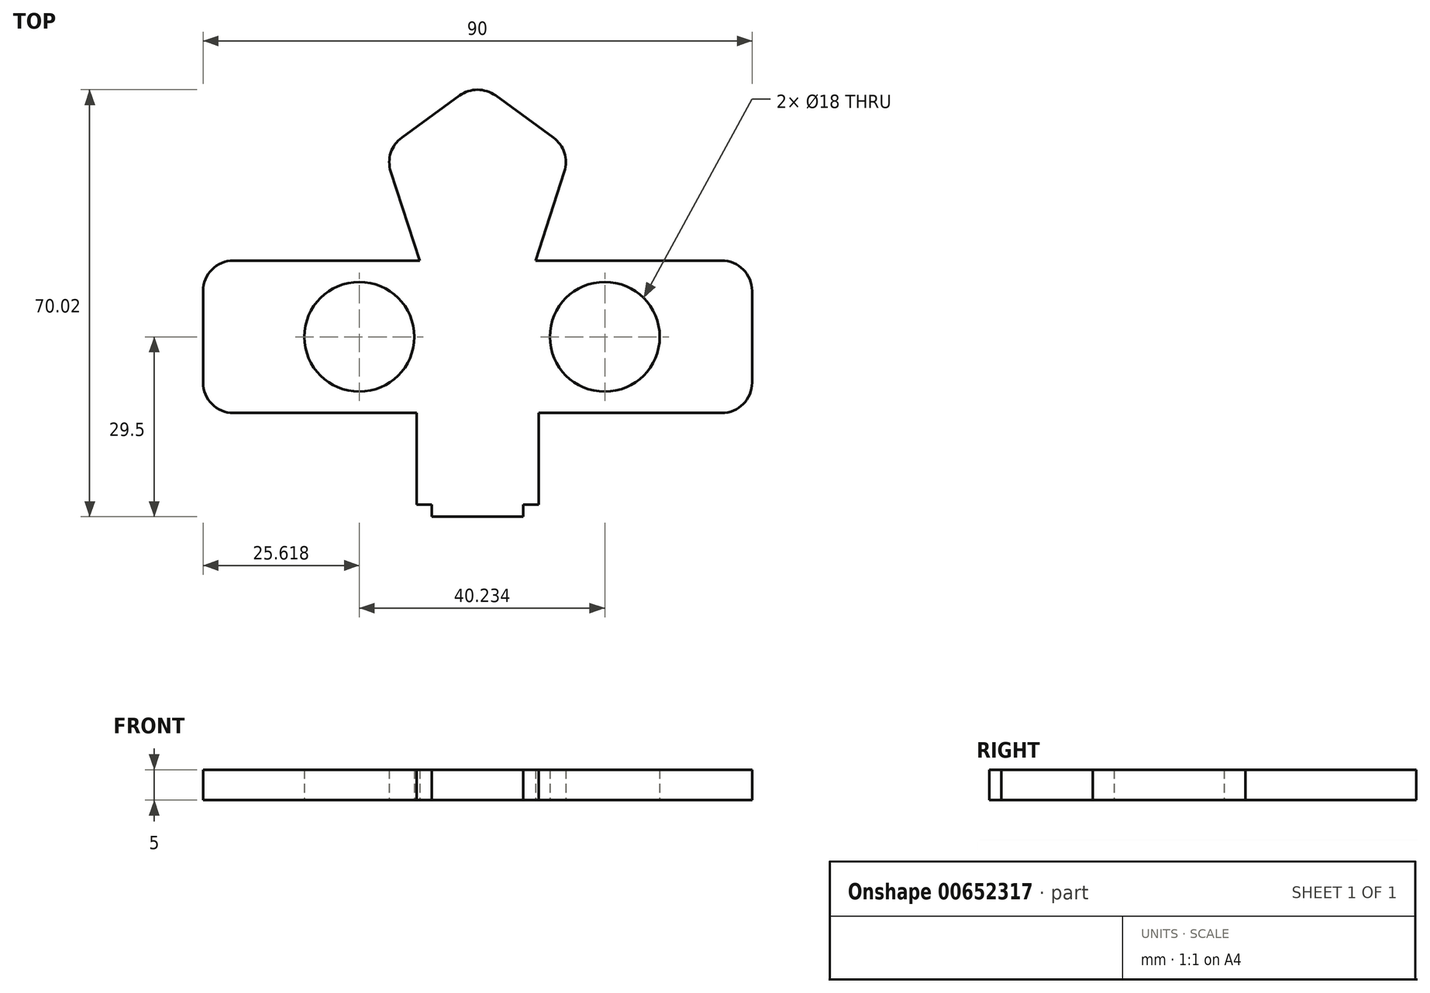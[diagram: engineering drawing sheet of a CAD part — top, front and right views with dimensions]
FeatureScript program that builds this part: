
annotation { "Feature Type Name" : "Feature", "Feature Type Description" : "" }
export const myFeature = defineFeature(function(context is Context, id is Id, definition is map)
    precondition{}
    {
        {
            var Q0;
            Q0=qCreatedBy(makeId("Top.planeOp"),FACE);
            var sketch = newSketch(context, id + "F0", { "sketchPlane" : qUnion([Q0])});
            skLineSegment(sketch, "E0.bottom", {"start": v(-40, 12.5) * mm, "end": v(40, 12.5) * mm});
            skLineSegment(sketch, "E0.top", {"start": v(-40, -12.5) * mm, "end": v(40, -12.5) * mm});
            skLineSegment(sketch, "E0.left", {"start": v(-45, 7.5) * mm, "end": v(-45, -7.5) * mm});
            skLineSegment(sketch, "E0.right", {"start": v(45, 7.5) * mm, "end": v(45, -7.5) * mm});
            skCircle(sketch, "E1", {"center": v(20.85, 0) * mm, "radius": 9 * mm});
            skCircle(sketch, "E2", {"center": v(-19.38, 0) * mm, "radius": 9 * mm});
            skLineSegment(sketch, "E3.bottom", {"start": v(-10, -12.5) * mm, "end": v(10, -12.5) * mm});
            skLineSegment(sketch, "E3.top", {"start": v(-10, -27.5) * mm, "end": v(10, -27.5) * mm});
            skLineSegment(sketch, "E3.left", {"start": v(-10, -12.5) * mm, "end": v(-10, -27.5) * mm});
            skLineSegment(sketch, "E3.right", {"start": v(10, -12.5) * mm, "end": v(10, -27.5) * mm});
            skLineSegment(sketch, "E4.bottom", {"start": v(-7.5, -27.5) * mm, "end": v(7.5, -27.5) * mm});
            skLineSegment(sketch, "E4.top", {"start": v(-7.5, -29.5) * mm, "end": v(7.5, -29.5) * mm});
            skLineSegment(sketch, "E4.left", {"start": v(-7.5, -27.5) * mm, "end": v(-7.5, -29.5) * mm});
            skLineSegment(sketch, "E4.right", {"start": v(7.5, -27.5) * mm, "end": v(7.5, -29.5) * mm});
            skLineSegment(sketch, "E5.0", {"start": v(9.49, 12.5) * mm, "end": v(-9.49, 12.5) * mm});
            skLineSegment(sketch, "E5.1", {"start": v(-9.49, 12.5) * mm, "end": v(-14.23, 27.1) * mm});
            skLineSegment(sketch, "E5.2", {"start": v(-12.41, 32.68) * mm, "end": v(-2.94, 39.56) * mm});
            skLineSegment(sketch, "E5.3", {"start": v(2.94, 39.56) * mm, "end": v(12.41, 32.68) * mm});
            skLineSegment(sketch, "E5.4", {"start": v(14.23, 27.1) * mm, "end": v(9.49, 12.5) * mm});
            skPoint(sketch, "E5.0.midPoint", {"position": v(0, 12.5) * mm});
            skPoint(sketch, "E6.visualSharp", {"position": v(-45, 12.5) * mm});
            skArc(sketch, "E6.filletArc", {"start": v(-40, 12.5) * mm, "mid": v(-43.54, 11.04) * mm, "end": v(-45, 7.5) * mm});
            skPoint(sketch, "E7.visualSharp", {"position": v(-45, -12.5) * mm});
            skArc(sketch, "E7.filletArc", {"start": v(-45, -7.5) * mm, "mid": v(-43.54, -11.04) * mm, "end": v(-40, -12.5) * mm});
            skPoint(sketch, "E8.visualSharp", {"position": v(45, -12.5) * mm});
            skArc(sketch, "E8.filletArc", {"start": v(40, -12.5) * mm, "mid": v(43.54, -11.04) * mm, "end": v(45, -7.5) * mm});
            skPoint(sketch, "E9.visualSharp", {"position": v(45, 12.5) * mm});
            skArc(sketch, "E9.filletArc", {"start": v(45, 7.5) * mm, "mid": v(43.54, 11.04) * mm, "end": v(40, 12.5) * mm});
            skPoint(sketch, "E10.visualSharp", {"position": v(0, 41.7) * mm});
            skArc(sketch, "E10.filletArc", {"start": v(2.94, 39.56) * mm, "mid": v(0, 40.52) * mm, "end": v(-2.94, 39.56) * mm});
            skPoint(sketch, "E11.visualSharp", {"position": v(-15.35, 30.55) * mm});
            skArc(sketch, "E11.filletArc", {"start": v(-12.41, 32.68) * mm, "mid": v(-14.23, 30.18) * mm, "end": v(-14.23, 27.1) * mm});
            skPoint(sketch, "E12.visualSharp", {"position": v(15.35, 30.55) * mm});
            skArc(sketch, "E12.filletArc", {"start": v(14.23, 27.1) * mm, "mid": v(14.23, 30.18) * mm, "end": v(12.41, 32.68) * mm});
            skSolve(sketch);
        }
        {
            var Q0;
            Q0=makeQuery(id+"F0.imprint","IMPRINT",FACE,{"disambiguationData":[TD([[makeQuery(id+"F0.imprint","IMPRINT",EDGE,{"derivedFrom":sQuery(id+"F0.wireOp",EDGE,"E0.left")}),1.0]])]});
            var Q1;
            {var subQ0=sQuery(id+"F0.wireOp",EDGE,"E5.1");Q1=makeQuery(id+"F0.imprint","IMPRINT",FACE,{"disambiguationData":[TD([[makeQuery(id+"F0.imprint","IMPRINT",EDGE,{"derivedFrom":subQ0}),-1.0]])]});}
            var Q2;
            {var subQ2=sQuery(id+"F0.wireOp",EDGE,"E3.left");Q2=makeQuery(id+"F0.imprint","IMPRINT",FACE,{"disambiguationData":[TD([[makeQuery(id+"F0.imprint","IMPRINT",EDGE,{"derivedFrom":subQ2}),1.0]])]});}
            var Q3;
            Q3=makeQuery(id+"F0.imprint","IMPRINT",FACE,{"disambiguationData":[TD([[makeQuery(id+"F0.imprint","IMPRINT",EDGE,{"derivedFrom":sQuery(id+"F0.wireOp",EDGE,"E4.top")}),1.0]])]});
            extrude(context, id + "F1", {"entities" : qUnion([Q0, Q1, Q2, Q3]), "depth" : 5 * mm, "offsetDistance" : 25 * mm});
        }
    });
